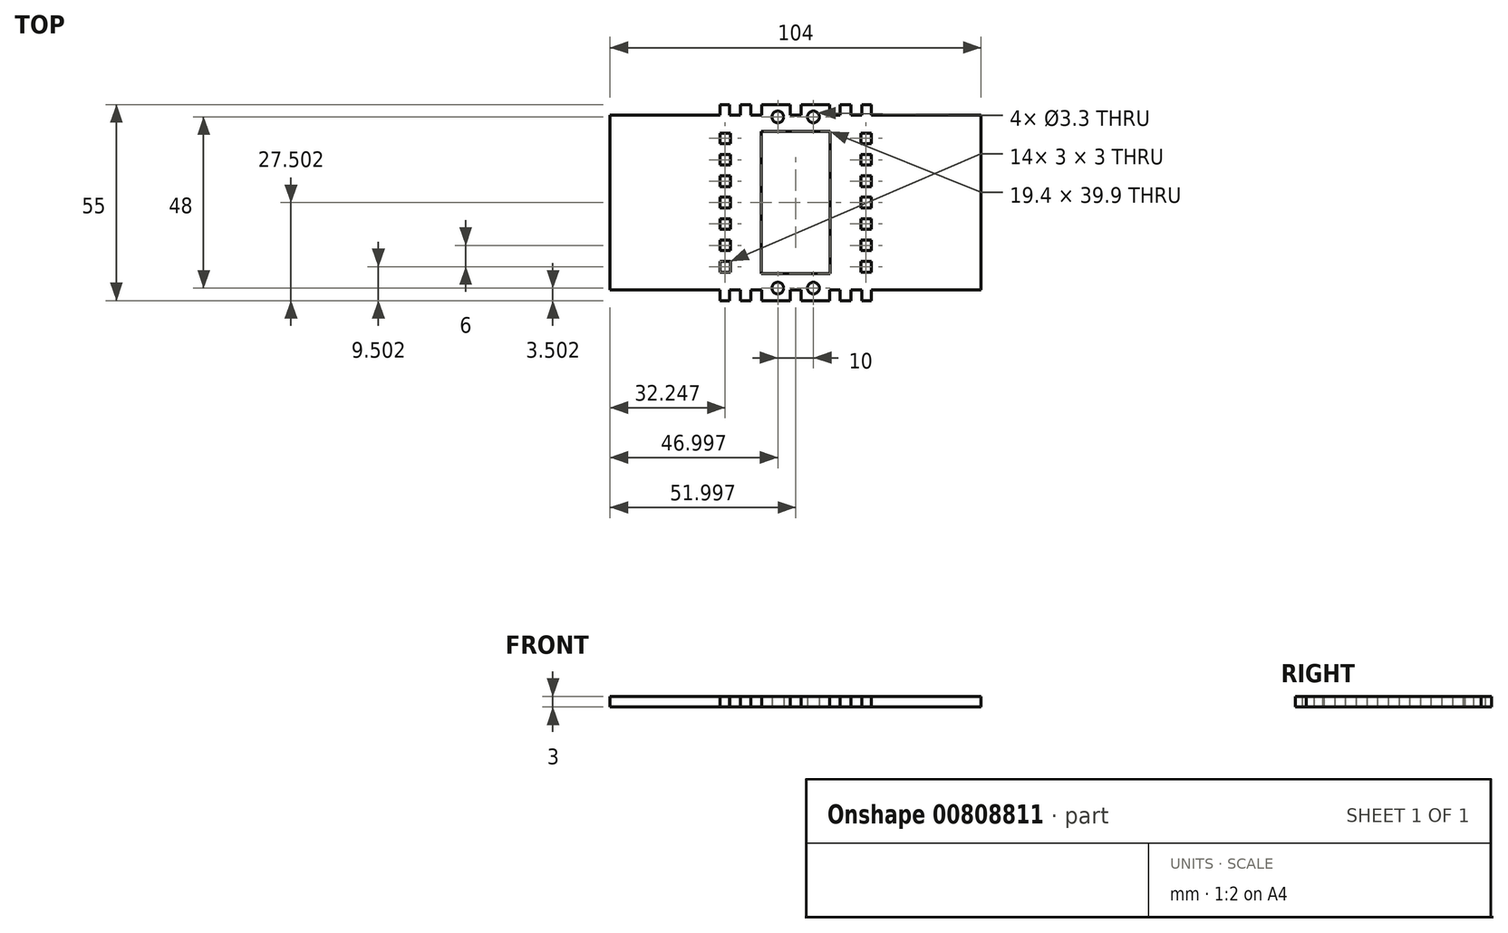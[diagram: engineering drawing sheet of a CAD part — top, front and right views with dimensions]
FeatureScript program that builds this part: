
annotation { "Feature Type Name" : "Feature", "Feature Type Description" : "" }
export const myFeature = defineFeature(function(context is Context, id is Id, definition is map)
    precondition{}
    {
        {
            var Q0;
            Q0=qCreatedBy(makeId("Top.planeOp"),FACE);
            var sketch = newSketch(context, id + "F0", { "sketchPlane" : qUnion([Q0])});
            skLineSegment(sketch, "E0.bottom", {"start": v(20.27, -26.13) * mm, "end": v(-22.23, -26.13) * mm});
            skLineSegment(sketch, "E0.top", {"start": v(20.27, 28.87) * mm, "end": v(-22.23, 28.87) * mm});
            skLineSegment(sketch, "E0.left", {"start": v(20.27, -26.13) * mm, "end": v(20.27, 28.87) * mm});
            skLineSegment(sketch, "E0.right", {"start": v(-22.23, -26.13) * mm, "end": v(-22.23, 28.87) * mm});
            skPoint(sketch, "E0.middle", {"position": v(-0.98, 1.37) * mm});
            skLineSegment(sketch, "E1.bottom", {"start": v(-19.23, -0.13) * mm, "end": v(-25.23, -0.13) * mm});
            skLineSegment(sketch, "E1.top", {"start": v(-19.23, 2.87) * mm, "end": v(-25.23, 2.87) * mm});
            skLineSegment(sketch, "E1.left", {"start": v(-19.23, -0.13) * mm, "end": v(-19.23, 2.87) * mm});
            skLineSegment(sketch, "E1.right", {"start": v(-25.23, -0.13) * mm, "end": v(-25.23, 2.87) * mm});
            skPoint(sketch, "E1.middle", {"position": v(-22.23, 1.37) * mm});
            skLineSegment(sketch, "E2.bottom", {"start": v(23.27, -0.13) * mm, "end": v(17.27, -0.13) * mm});
            skLineSegment(sketch, "E2.top", {"start": v(23.27, 2.87) * mm, "end": v(17.27, 2.87) * mm});
            skLineSegment(sketch, "E2.left", {"start": v(23.27, -0.13) * mm, "end": v(23.27, 2.87) * mm});
            skLineSegment(sketch, "E2.right", {"start": v(17.27, -0.13) * mm, "end": v(17.27, 2.87) * mm});
            skPoint(sketch, "E2.middle", {"position": v(20.27, 1.37) * mm});
            skLineSegment(sketch, "E3.bottom", {"start": v(0.52, -29.13) * mm, "end": v(-2.48, -29.13) * mm});
            skLineSegment(sketch, "E3.top", {"start": v(0.52, -23.13) * mm, "end": v(-2.48, -23.13) * mm});
            skLineSegment(sketch, "E3.left", {"start": v(0.52, -29.13) * mm, "end": v(0.52, -23.13) * mm});
            skLineSegment(sketch, "E3.right", {"start": v(-2.48, -29.13) * mm, "end": v(-2.48, -23.13) * mm});
            skPoint(sketch, "E3.middle", {"position": v(-0.98, -26.13) * mm});
            skLineSegment(sketch, "E4.bottom", {"start": v(0.52, 25.87) * mm, "end": v(-2.48, 25.87) * mm});
            skLineSegment(sketch, "E4.top", {"start": v(0.52, 31.87) * mm, "end": v(-2.48, 31.87) * mm});
            skLineSegment(sketch, "E4.left", {"start": v(0.52, 25.87) * mm, "end": v(0.52, 31.87) * mm});
            skLineSegment(sketch, "E4.right", {"start": v(-2.48, 25.87) * mm, "end": v(-2.48, 31.87) * mm});
            skPoint(sketch, "E4.middle", {"position": v(-0.98, 28.87) * mm});
            skLineSegment(sketch, "E5.bottom", {"start": v(-10.68, -18.58) * mm, "end": v(8.72, -18.58) * mm});
            skLineSegment(sketch, "E5.top", {"start": v(-10.68, 21.32) * mm, "end": v(8.72, 21.32) * mm});
            skLineSegment(sketch, "E5.left", {"start": v(-10.68, -18.58) * mm, "end": v(-10.68, 21.32) * mm});
            skLineSegment(sketch, "E5.right", {"start": v(8.72, -18.58) * mm, "end": v(8.72, 21.32) * mm});
            skLineSegment(sketch, "E6.bottom", {"start": v(-19.23, -6.13) * mm, "end": v(-25.23, -6.13) * mm});
            skLineSegment(sketch, "E6.top", {"start": v(-19.23, -3.13) * mm, "end": v(-25.23, -3.13) * mm});
            skLineSegment(sketch, "E6.left", {"start": v(-19.23, -6.13) * mm, "end": v(-19.23, -3.13) * mm});
            skLineSegment(sketch, "E6.right", {"start": v(-25.23, -6.13) * mm, "end": v(-25.23, -3.13) * mm});
            skPoint(sketch, "E6.middle", {"position": v(-22.23, -4.63) * mm});
            skLineSegment(sketch, "E7.bottom", {"start": v(-19.23, 5.87) * mm, "end": v(-25.23, 5.87) * mm});
            skLineSegment(sketch, "E7.top", {"start": v(-19.23, 8.87) * mm, "end": v(-25.23, 8.87) * mm});
            skLineSegment(sketch, "E7.left", {"start": v(-19.23, 5.87) * mm, "end": v(-19.23, 8.87) * mm});
            skLineSegment(sketch, "E7.right", {"start": v(-25.23, 5.87) * mm, "end": v(-25.23, 8.87) * mm});
            skPoint(sketch, "E7.middle", {"position": v(-22.23, 7.37) * mm});
            skLineSegment(sketch, "E8.bottom", {"start": v(-19.23, 11.87) * mm, "end": v(-25.23, 11.87) * mm});
            skLineSegment(sketch, "E8.top", {"start": v(-19.23, 14.87) * mm, "end": v(-25.23, 14.87) * mm});
            skLineSegment(sketch, "E8.left", {"start": v(-19.23, 11.87) * mm, "end": v(-19.23, 14.87) * mm});
            skLineSegment(sketch, "E8.right", {"start": v(-25.23, 11.87) * mm, "end": v(-25.23, 14.87) * mm});
            skPoint(sketch, "E8.middle", {"position": v(-22.23, 13.37) * mm});
            skLineSegment(sketch, "E9.bottom", {"start": v(-19.23, -12.13) * mm, "end": v(-25.23, -12.13) * mm});
            skLineSegment(sketch, "E9.top", {"start": v(-19.23, -9.13) * mm, "end": v(-25.23, -9.13) * mm});
            skLineSegment(sketch, "E9.left", {"start": v(-19.23, -12.13) * mm, "end": v(-19.23, -9.13) * mm});
            skLineSegment(sketch, "E9.right", {"start": v(-25.23, -12.13) * mm, "end": v(-25.23, -9.13) * mm});
            skPoint(sketch, "E9.middle", {"position": v(-22.23, -10.63) * mm});
            skLineSegment(sketch, "E10.bottom", {"start": v(-19.23, 17.87) * mm, "end": v(-25.23, 17.87) * mm});
            skLineSegment(sketch, "E10.top", {"start": v(-19.23, 20.87) * mm, "end": v(-25.23, 20.87) * mm});
            skLineSegment(sketch, "E10.left", {"start": v(-19.23, 17.87) * mm, "end": v(-19.23, 20.87) * mm});
            skLineSegment(sketch, "E10.right", {"start": v(-25.23, 17.87) * mm, "end": v(-25.23, 20.87) * mm});
            skPoint(sketch, "E10.middle", {"position": v(-22.23, 19.37) * mm});
            skLineSegment(sketch, "E11.bottom", {"start": v(-19.23, -18.13) * mm, "end": v(-25.23, -18.13) * mm});
            skLineSegment(sketch, "E11.top", {"start": v(-19.23, -15.13) * mm, "end": v(-25.23, -15.13) * mm});
            skLineSegment(sketch, "E11.left", {"start": v(-19.23, -18.13) * mm, "end": v(-19.23, -15.13) * mm});
            skLineSegment(sketch, "E11.right", {"start": v(-25.23, -18.13) * mm, "end": v(-25.23, -15.13) * mm});
            skPoint(sketch, "E11.middle", {"position": v(-22.23, -16.63) * mm});
            skLineSegment(sketch, "E12", {"start": v(-0.98, 1.37) * mm, "end": v(-0.98, 4.83) * mm});
            skLineSegment(sketch, "E13.MirrorCS", {"start": v(23.27, 5.87) * mm, "end": v(23.27, 8.87) * mm});
            skLineSegment(sketch, "E14.MirrorCS", {"start": v(23.27, -12.13) * mm, "end": v(23.27, -9.13) * mm});
            skLineSegment(sketch, "E15.MirrorCS", {"start": v(17.27, -12.13) * mm, "end": v(17.27, -9.13) * mm});
            skLineSegment(sketch, "E16.MirrorCS", {"start": v(17.27, 11.87) * mm, "end": v(17.27, 14.87) * mm});
            skLineSegment(sketch, "E17.MirrorCS", {"start": v(17.27, 5.87) * mm, "end": v(17.27, 8.87) * mm});
            skLineSegment(sketch, "E18.MirrorCS", {"start": v(17.27, 17.87) * mm, "end": v(17.27, 20.87) * mm});
            skLineSegment(sketch, "E19.MirrorCS", {"start": v(23.27, 11.87) * mm, "end": v(23.27, 14.87) * mm});
            skLineSegment(sketch, "E20.MirrorCS", {"start": v(23.27, 17.87) * mm, "end": v(23.27, 20.87) * mm});
            skLineSegment(sketch, "E21.MirrorCS", {"start": v(17.27, 11.87) * mm, "end": v(23.27, 11.87) * mm});
            skLineSegment(sketch, "E22.MirrorCS", {"start": v(17.27, -3.13) * mm, "end": v(23.27, -3.13) * mm});
            skLineSegment(sketch, "E23.MirrorCS", {"start": v(17.27, 20.87) * mm, "end": v(23.27, 20.87) * mm});
            skLineSegment(sketch, "E24.MirrorCS", {"start": v(17.27, -0.13) * mm, "end": v(23.27, -0.13) * mm});
            skLineSegment(sketch, "E25.MirrorCS", {"start": v(17.27, 2.87) * mm, "end": v(23.27, 2.87) * mm});
            skLineSegment(sketch, "E26.MirrorCS", {"start": v(17.27, 17.87) * mm, "end": v(23.27, 17.87) * mm});
            skLineSegment(sketch, "E27.MirrorCS", {"start": v(17.27, 14.87) * mm, "end": v(23.27, 14.87) * mm});
            skLineSegment(sketch, "E28.MirrorCS", {"start": v(17.27, -9.13) * mm, "end": v(23.27, -9.13) * mm});
            skLineSegment(sketch, "E29.MirrorCS", {"start": v(17.27, 5.87) * mm, "end": v(23.27, 5.87) * mm});
            skLineSegment(sketch, "E30.MirrorCS", {"start": v(17.27, -18.13) * mm, "end": v(23.27, -18.13) * mm});
            skLineSegment(sketch, "E31.MirrorCS", {"start": v(17.27, 8.87) * mm, "end": v(23.27, 8.87) * mm});
            skLineSegment(sketch, "E32.MirrorCS", {"start": v(17.27, -12.13) * mm, "end": v(23.27, -12.13) * mm});
            skLineSegment(sketch, "E33.MirrorCS", {"start": v(23.27, -18.13) * mm, "end": v(23.27, -15.13) * mm});
            skLineSegment(sketch, "E34.MirrorCS", {"start": v(17.27, -6.13) * mm, "end": v(23.27, -6.13) * mm});
            skPoint(sketch, "E35.MirrorP", {"position": v(20.27, -4.63) * mm});
            skPoint(sketch, "E36.MirrorP", {"position": v(20.27, 7.37) * mm});
            skLineSegment(sketch, "E37.MirrorCS", {"start": v(17.27, -18.13) * mm, "end": v(17.27, -15.13) * mm});
            skPoint(sketch, "E38.MirrorP", {"position": v(20.27, 19.37) * mm});
            skLineSegment(sketch, "E39.MirrorCS", {"start": v(17.27, -6.13) * mm, "end": v(17.27, -3.13) * mm});
            skPoint(sketch, "E40.MirrorP", {"position": v(20.27, 13.37) * mm});
            skLineSegment(sketch, "E41.MirrorCS", {"start": v(17.27, -15.13) * mm, "end": v(23.27, -15.13) * mm});
            skPoint(sketch, "E42.MirrorP", {"position": v(20.27, -10.63) * mm});
            skLineSegment(sketch, "E43.MirrorCS", {"start": v(23.27, -6.13) * mm, "end": v(23.27, -3.13) * mm});
            skPoint(sketch, "E44.MirrorP", {"position": v(20.27, -16.63) * mm});
            skCircle(sketch, "E45", {"center": v(4.02, 25.37) * mm, "radius": 1.65 * mm});
            skCircle(sketch, "E46", {"center": v(-5.98, 25.37) * mm, "radius": 1.65 * mm});
            skCircle(sketch, "E47", {"center": v(-5.98, -22.63) * mm, "radius": 1.65 * mm});
            skCircle(sketch, "E48", {"center": v(4.02, -22.63) * mm, "radius": 1.65 * mm});
            skLineSegment(sketch, "E49.bottom", {"start": v(-13.48, 25.87) * mm, "end": v(-10.48, 25.87) * mm});
            skLineSegment(sketch, "E49.top", {"start": v(-13.48, 31.87) * mm, "end": v(-10.48, 31.87) * mm});
            skLineSegment(sketch, "E49.left", {"start": v(-13.48, 25.87) * mm, "end": v(-13.48, 31.87) * mm});
            skLineSegment(sketch, "E49.right", {"start": v(-10.48, 25.87) * mm, "end": v(-10.48, 31.87) * mm});
            skPoint(sketch, "E49.middle", {"position": v(-11.98, 28.87) * mm});
            skLineSegment(sketch, "E50.bottom", {"start": v(-16.48, 25.87) * mm, "end": v(-19.48, 25.87) * mm});
            skLineSegment(sketch, "E50.top", {"start": v(-16.48, 31.87) * mm, "end": v(-19.48, 31.87) * mm});
            skLineSegment(sketch, "E50.left", {"start": v(-16.48, 25.87) * mm, "end": v(-16.48, 31.87) * mm});
            skLineSegment(sketch, "E50.right", {"start": v(-19.48, 25.87) * mm, "end": v(-19.48, 31.87) * mm});
            skPoint(sketch, "E50.middle", {"position": v(-17.98, 28.87) * mm});
            skLineSegment(sketch, "E51.MirrorCS", {"start": v(8.52, 25.87) * mm, "end": v(8.52, 31.87) * mm});
            skLineSegment(sketch, "E52.MirrorCS", {"start": v(11.52, 31.87) * mm, "end": v(8.52, 31.87) * mm});
            skLineSegment(sketch, "E53.MirrorCS", {"start": v(11.52, 25.87) * mm, "end": v(11.52, 31.87) * mm});
            skLineSegment(sketch, "E54.MirrorCS", {"start": v(11.52, 25.87) * mm, "end": v(8.52, 25.87) * mm});
            skLineSegment(sketch, "E55.MirrorCS", {"start": v(14.52, 25.87) * mm, "end": v(17.52, 25.87) * mm});
            skLineSegment(sketch, "E56.MirrorCS", {"start": v(14.52, 25.87) * mm, "end": v(14.52, 31.87) * mm});
            skLineSegment(sketch, "E57.MirrorCS", {"start": v(14.52, 31.87) * mm, "end": v(17.52, 31.87) * mm});
            skLineSegment(sketch, "E58.MirrorCS", {"start": v(17.52, 25.87) * mm, "end": v(17.52, 31.87) * mm});
            skPoint(sketch, "E59.MirrorP", {"position": v(10.02, 28.87) * mm});
            skPoint(sketch, "E60.MirrorP", {"position": v(16.02, 28.87) * mm});
            skLineSegment(sketch, "E61", {"start": v(-0.98, 1.37) * mm, "end": v(4.17, 1.37) * mm});
            skLineSegment(sketch, "E62.MirrorCS", {"start": v(-16.48, -29.13) * mm, "end": v(-19.48, -29.13) * mm});
            skLineSegment(sketch, "E63.MirrorCS", {"start": v(-13.48, -29.13) * mm, "end": v(-10.48, -29.13) * mm});
            skLineSegment(sketch, "E64.MirrorCS", {"start": v(-16.48, -23.13) * mm, "end": v(-19.48, -23.13) * mm});
            skLineSegment(sketch, "E65.MirrorCS", {"start": v(14.52, -23.13) * mm, "end": v(17.52, -23.13) * mm});
            skLineSegment(sketch, "E66.MirrorCS", {"start": v(11.52, -23.13) * mm, "end": v(8.52, -23.13) * mm});
            skLineSegment(sketch, "E67.MirrorCS", {"start": v(11.52, -29.13) * mm, "end": v(8.52, -29.13) * mm});
            skLineSegment(sketch, "E68.MirrorCS", {"start": v(14.52, -29.13) * mm, "end": v(17.52, -29.13) * mm});
            skLineSegment(sketch, "E69.MirrorCS", {"start": v(-13.48, -23.13) * mm, "end": v(-10.48, -23.13) * mm});
            skLineSegment(sketch, "E70.MirrorCS", {"start": v(-10.48, -23.13) * mm, "end": v(-10.48, -29.13) * mm});
            skLineSegment(sketch, "E71.MirrorCS", {"start": v(-19.48, -23.13) * mm, "end": v(-19.48, -29.13) * mm});
            skLineSegment(sketch, "E72.MirrorCS", {"start": v(8.52, -23.13) * mm, "end": v(8.52, -29.13) * mm});
            skLineSegment(sketch, "E73.MirrorCS", {"start": v(-16.48, -23.13) * mm, "end": v(-16.48, -29.13) * mm});
            skLineSegment(sketch, "E74.MirrorCS", {"start": v(11.52, -23.13) * mm, "end": v(11.52, -29.13) * mm});
            skLineSegment(sketch, "E75.MirrorCS", {"start": v(-13.48, -23.13) * mm, "end": v(-13.48, -29.13) * mm});
            skLineSegment(sketch, "E76.MirrorCS", {"start": v(20.27, 28.87) * mm, "end": v(20.27, -26.13) * mm});
            skLineSegment(sketch, "E77.MirrorCS", {"start": v(14.52, -23.13) * mm, "end": v(14.52, -29.13) * mm});
            skLineSegment(sketch, "E78.MirrorCS", {"start": v(17.52, -23.13) * mm, "end": v(17.52, -29.13) * mm});
            skLineSegment(sketch, "E79.MirrorCS", {"start": v(-2.48, -23.13) * mm, "end": v(-2.48, -29.13) * mm});
            skLineSegment(sketch, "E80.MirrorCS", {"start": v(0.52, -23.13) * mm, "end": v(0.52, -29.13) * mm});
            skPoint(sketch, "E81.MirrorP", {"position": v(10.02, -26.13) * mm});
            skPoint(sketch, "E82.MirrorP", {"position": v(-17.98, -26.13) * mm});
            skPoint(sketch, "E83.MirrorP", {"position": v(-11.98, -26.13) * mm});
            skPoint(sketch, "E84.MirrorP", {"position": v(16.02, -26.13) * mm});
            skLineSegment(sketch, "E85.MirrorCS", {"start": v(-22.23, 28.87) * mm, "end": v(-22.23, -26.13) * mm});
            skSolve(sketch);
        }
        {
            var Q0;
            {var subQ103=sQuery(id+"F0.wireOp",EDGE,"E1.left");Q0=makeQuery(id+"F0.imprint","IMPRINT",FACE,{"disambiguationData":[TD([[makeQuery(id+"F0.imprint","IMPRINT",EDGE,{"derivedFrom":subQ103}),-1.0]])]});}
            extrude(context, id + "F1", {"entities" : qUnion([Q0]), "depth" : 3 * mm, "offsetDistance" : 25 * mm});
        }
        {
            var Q0;
            Q0=makeQuery(id+"F1.opExtrude","CAP_FACE",FACE,{"disambiguationData":[OSD([sQuery(id+"F0.wireOp",EDGE,"E0.top"),sQuery(id+"F0.wireOp",EDGE,"E1.bottom"),sQuery(id+"F0.wireOp",EDGE,"E1.top"),sQuery(id+"F0.wireOp",EDGE,"E1.left"),sQuery(id+"F0.wireOp",EDGE,"E4.bottom"),sQuery(id+"F0.wireOp",EDGE,"E4.left"),sQuery(id+"F0.wireOp",EDGE,"E4.right"),sQuery(id+"F0.wireOp",EDGE,"E5.bottom"),sQuery(id+"F0.wireOp",EDGE,"E5.top"),sQuery(id+"F0.wireOp",EDGE,"E5.left"),sQuery(id+"F0.wireOp",EDGE,"E5.right"),sQuery(id+"F0.wireOp",EDGE,"E6.bottom"),sQuery(id+"F0.wireOp",EDGE,"E6.top"),sQuery(id+"F0.wireOp",EDGE,"E6.left"),sQuery(id+"F0.wireOp",EDGE,"E7.bottom"),sQuery(id+"F0.wireOp",EDGE,"E7.top"),sQuery(id+"F0.wireOp",EDGE,"E7.left"),sQuery(id+"F0.wireOp",EDGE,"E8.bottom"),sQuery(id+"F0.wireOp",EDGE,"E8.top"),sQuery(id+"F0.wireOp",EDGE,"E8.left"),sQuery(id+"F0.wireOp",EDGE,"E9.bottom"),sQuery(id+"F0.wireOp",EDGE,"E9.top"),sQuery(id+"F0.wireOp",EDGE,"E9.left"),sQuery(id+"F0.wireOp",EDGE,"E10.bottom"),sQuery(id+"F0.wireOp",EDGE,"E10.top"),sQuery(id+"F0.wireOp",EDGE,"E10.left"),sQuery(id+"F0.wireOp",EDGE,"E11.bottom"),sQuery(id+"F0.wireOp",EDGE,"E11.top"),sQuery(id+"F0.wireOp",EDGE,"E11.left"),sQuery(id+"F0.wireOp",EDGE,"E15.MirrorCS"),sQuery(id+"F0.wireOp",EDGE,"E16.MirrorCS"),sQuery(id+"F0.wireOp",EDGE,"E2.right"),sQuery(id+"F0.wireOp",EDGE,"E17.MirrorCS"),sQuery(id+"F0.wireOp",EDGE,"E18.MirrorCS"),sQuery(id+"F0.wireOp",EDGE,"E21.MirrorCS"),sQuery(id+"F0.wireOp",EDGE,"E22.MirrorCS"),sQuery(id+"F0.wireOp",EDGE,"E23.MirrorCS"),sQuery(id+"F0.wireOp",EDGE,"E24.MirrorCS"),sQuery(id+"F0.wireOp",EDGE,"E25.MirrorCS"),sQuery(id+"F0.wireOp",EDGE,"E26.MirrorCS"),sQuery(id+"F0.wireOp",EDGE,"E27.MirrorCS"),sQuery(id+"F0.wireOp",EDGE,"E28.MirrorCS"),sQuery(id+"F0.wireOp",EDGE,"E29.MirrorCS"),sQuery(id+"F0.wireOp",EDGE,"E30.MirrorCS"),sQuery(id+"F0.wireOp",EDGE,"E31.MirrorCS"),sQuery(id+"F0.wireOp",EDGE,"E32.MirrorCS"),sQuery(id+"F0.wireOp",EDGE,"E34.MirrorCS"),sQuery(id+"F0.wireOp",EDGE,"E37.MirrorCS"),sQuery(id+"F0.wireOp",EDGE,"E39.MirrorCS"),sQuery(id+"F0.wireOp",EDGE,"E41.MirrorCS"),sQuery(id+"F0.wireOp",EDGE,"E45"),sQuery(id+"F0.wireOp",EDGE,"E46"),sQuery(id+"F0.wireOp",EDGE,"E49.bottom"),sQuery(id+"F0.wireOp",EDGE,"E49.left"),sQuery(id+"F0.wireOp",EDGE,"E49.right"),sQuery(id+"F0.wireOp",EDGE,"E50.bottom"),sQuery(id+"F0.wireOp",EDGE,"E50.left"),sQuery(id+"F0.wireOp",EDGE,"E50.right"),sQuery(id+"F0.wireOp",EDGE,"E51.MirrorCS"),sQuery(id+"F0.wireOp",EDGE,"E53.MirrorCS"),sQuery(id+"F0.wireOp",EDGE,"E54.MirrorCS"),sQuery(id+"F0.wireOp",EDGE,"E55.MirrorCS"),sQuery(id+"F0.wireOp",EDGE,"E56.MirrorCS"),sQuery(id+"F0.wireOp",EDGE,"E58.MirrorCS"),sQuery(id+"F0.wireOp",EDGE,"E64.MirrorCS"),sQuery(id+"F0.wireOp",EDGE,"E65.MirrorCS"),sQuery(id+"F0.wireOp",EDGE,"E3.top"),sQuery(id+"F0.wireOp",EDGE,"E66.MirrorCS"),sQuery(id+"F0.wireOp",EDGE,"E69.MirrorCS"),sQuery(id+"F0.wireOp",EDGE,"E70.MirrorCS"),sQuery(id+"F0.wireOp",EDGE,"E71.MirrorCS"),sQuery(id+"F0.wireOp",EDGE,"E72.MirrorCS"),sQuery(id+"F0.wireOp",EDGE,"E73.MirrorCS"),sQuery(id+"F0.wireOp",EDGE,"E74.MirrorCS"),sQuery(id+"F0.wireOp",EDGE,"E75.MirrorCS"),sQuery(id+"F0.wireOp",EDGE,"E77.MirrorCS"),sQuery(id+"F0.wireOp",EDGE,"E78.MirrorCS"),sQuery(id+"F0.wireOp",EDGE,"E79.MirrorCS"),sQuery(id+"F0.wireOp",EDGE,"E80.MirrorCS"),sQuery(id+"F0.wireOp",EDGE,"E76.MirrorCS"),sQuery(id+"F0.wireOp",EDGE,"E48"),sQuery(id+"F0.wireOp",EDGE,"E85.MirrorCS"),sQuery(id+"F0.wireOp",EDGE,"E0.bottom"),sQuery(id+"F0.wireOp",EDGE,"E47")])],"isStart":false});
            var sketch = newSketch(context, id + "F2", { "sketchPlane" : qUnion([Q0])});
            skLineSegment(sketch, "E86.bottom", {"start": v(51.02, -23.13) * mm, "end": v(-52.98, -23.13) * mm});
            skLineSegment(sketch, "E86.top", {"start": v(51.02, 25.87) * mm, "end": v(-52.98, 25.87) * mm});
            skLineSegment(sketch, "E86.left", {"start": v(51.02, -23.13) * mm, "end": v(51.02, 25.87) * mm});
            skLineSegment(sketch, "E86.right", {"start": v(-52.98, -23.13) * mm, "end": v(-52.98, 25.87) * mm});
            skPoint(sketch, "E86.middle", {"position": v(-0.98, 1.37) * mm});
            skPoint(sketch, "E86.middle.positionSnap0", {"position": v(-0.98, 21.32) * mm});
            skPoint(sketch, "E86.cornerSnap0", {"position": v(14.52, -23.13) * mm});
            skPoint(sketch, "E86.centerSnap0", {"position": v(-0.98, 21.32) * mm});
            skLineSegment(sketch, "E87", {"start": v(-22.23, -26.13) * mm, "end": v(-22.23, 28.87) * mm});
            skLineSegment(sketch, "E88", {"start": v(-22.23, 28.87) * mm, "end": v(20.27, 28.87) * mm});
            skLineSegment(sketch, "E89", {"start": v(20.27, 28.87) * mm, "end": v(20.27, -26.13) * mm});
            skSolve(sketch);
        }
        {
            var Q0;
            {var subQ11=sQuery(id+"F2.wireOp",EDGE,"E86.right");Q0=makeQuery(id+"F2.imprint","IMPRINT",FACE,{"disambiguationData":[TD([[makeQuery(id+"F2.imprint","IMPRINT",EDGE,{"derivedFrom":subQ11}),-1.0]])]});}
            var Q1;
            {var subQ5=sQuery(id+"F2.wireOp",EDGE,"E86.left");Q1=makeQuery(id+"F2.imprint","IMPRINT",FACE,{"disambiguationData":[TD([[makeQuery(id+"F2.imprint","IMPRINT",EDGE,{"derivedFrom":subQ5}),1.0]])]});}
            extrude(context, id + "F3", {"entities" : qUnion([Q0, Q1]), "operationType" : NewBodyOperationType.ADD, "oppositeDirection" : true, "depth" : 3 * mm, "offsetDistance" : 25 * mm});
        }
    });
